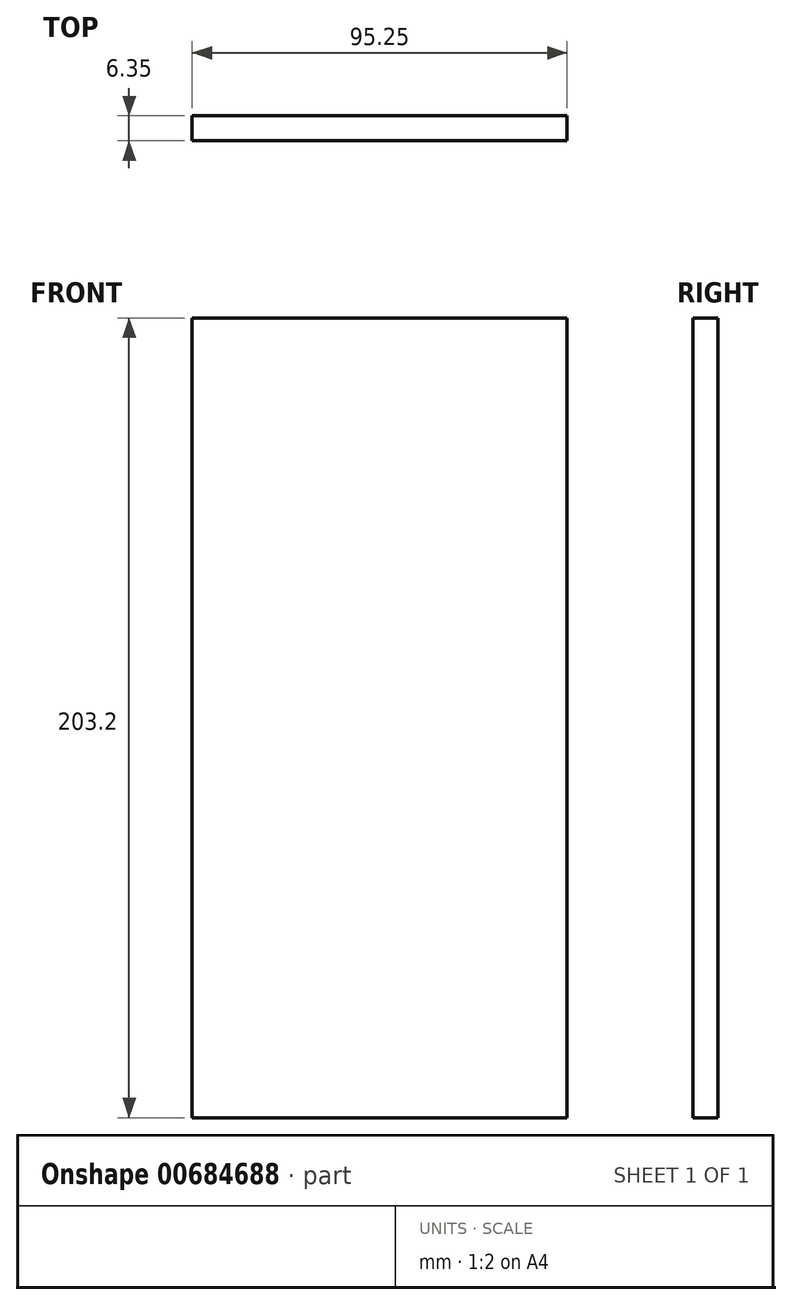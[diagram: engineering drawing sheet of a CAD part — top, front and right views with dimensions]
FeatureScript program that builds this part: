
annotation { "Feature Type Name" : "Feature", "Feature Type Description" : "" }
export const myFeature = defineFeature(function(context is Context, id is Id, definition is map)
    precondition{}
    {
        {
            var Q0;
            Q0=qCreatedBy(makeId("Front.planeOp"),FACE);
            var sketch = newSketch(context, id + "F0", { "sketchPlane" : qUnion([Q0])});
            skLineSegment(sketch, "E0.bottom", {"start": v(-45.03, 168.09) * mm, "end": v(50.22, 168.09) * mm});
            skLineSegment(sketch, "E0.top", {"start": v(-45.03, -35.11) * mm, "end": v(50.22, -35.11) * mm});
            skLineSegment(sketch, "E0.left", {"start": v(-45.03, 168.09) * mm, "end": v(-45.03, -35.11) * mm});
            skLineSegment(sketch, "E0.right", {"start": v(50.22, 168.09) * mm, "end": v(50.22, -35.11) * mm});
            skSolve(sketch);
        }
        {
            var Q0;
            Q0=qSketchRegion(id+"F0",true);
            extrude(context, id + "F1", {"entities" : qUnion([Q0]), "depth" : 6.35 * mm, "offsetDistance" : 25.4 * mm});
        }
    });
